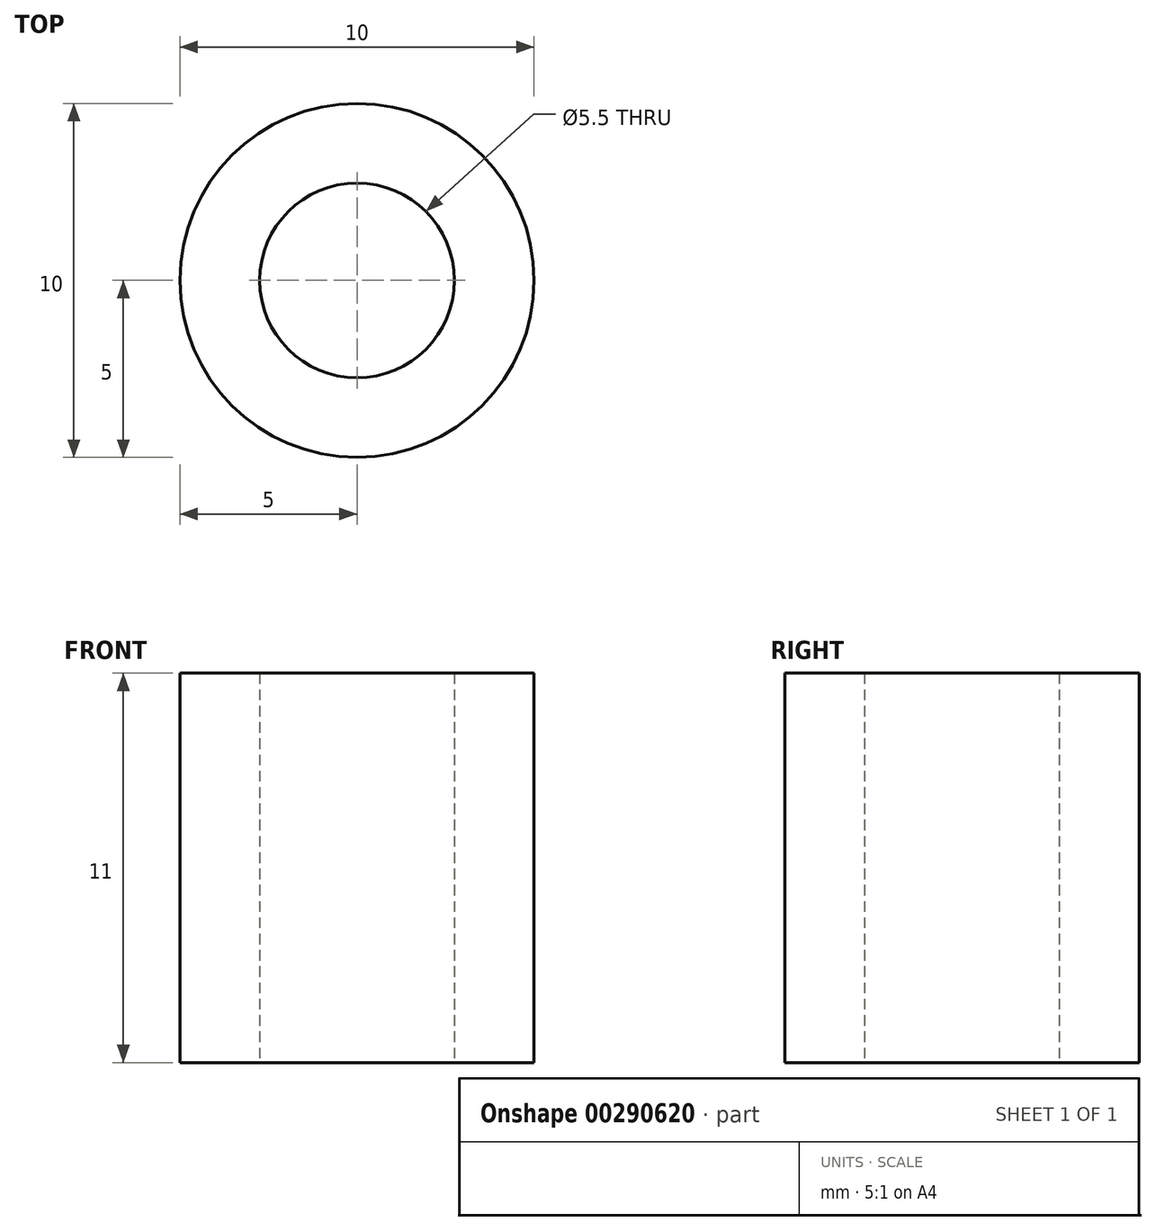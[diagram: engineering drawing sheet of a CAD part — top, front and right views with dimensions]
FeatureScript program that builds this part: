
annotation { "Feature Type Name" : "Feature", "Feature Type Description" : "" }
export const myFeature = defineFeature(function(context is Context, id is Id, definition is map)
    precondition{}
    {
        {
            var Q0;
            Q0=qCreatedBy(makeId("Top.planeOp"),FACE);
            var sketch = newSketch(context, id + "F0", { "sketchPlane" : qUnion([Q0])});
            skCircle(sketch, "E0", {"center": v(0, 0) * mm, "radius": 2.75 * mm});
            skCircle(sketch, "E1", {"center": v(0, 0) * mm, "radius": 5 * mm});
            skSolve(sketch);
        }
        {
            var Q0;
            Q0 = qSketchRegion(id + "F0", true);
            extrude(context, id + "F1", {"entities" : qUnion([Q0]), "depth" : 11 * mm});
        }
    });
